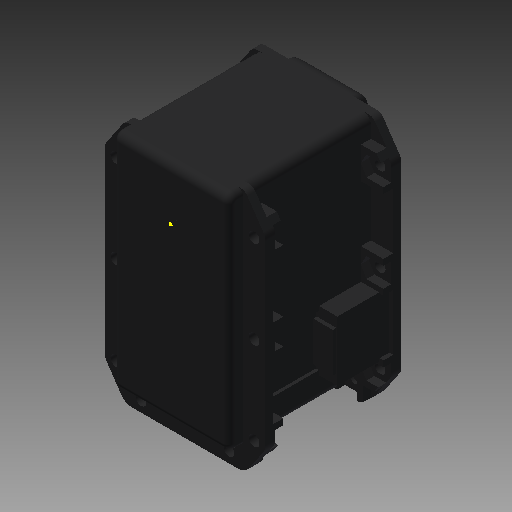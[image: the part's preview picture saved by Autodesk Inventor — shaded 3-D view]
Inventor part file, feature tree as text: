
AUTODESK INVENTOR PART (.ipt)
format: ipt  version: 2019 (Build 230136000, 136)  size: 652,800 bytes
history: native  units: in
note: dims shown in document units (in); Inventor stores cm internally (conversion verified against a paired STEP export)
features: sketch x3, other x1, extrude x1, imported_body x1
ambient origin geometry x8: Origin, YZ Plane, XZ Plane, XY Plane, X Axis, Y Axis, Z Axis, Center Point
bodies: Solid1 (feature_tree)
feature tree (6):
  other  "MX-64T1"
  sketch  "Sketch1"  dims[d2=0.1575in d3=0.0in]
  sketch  "Sketch2"  dims[d4=0.0in]
  extrude  "Extrusion1"  Depth=0.0in
  imported_body  "Base1"
  sketch  "Sketch3"
